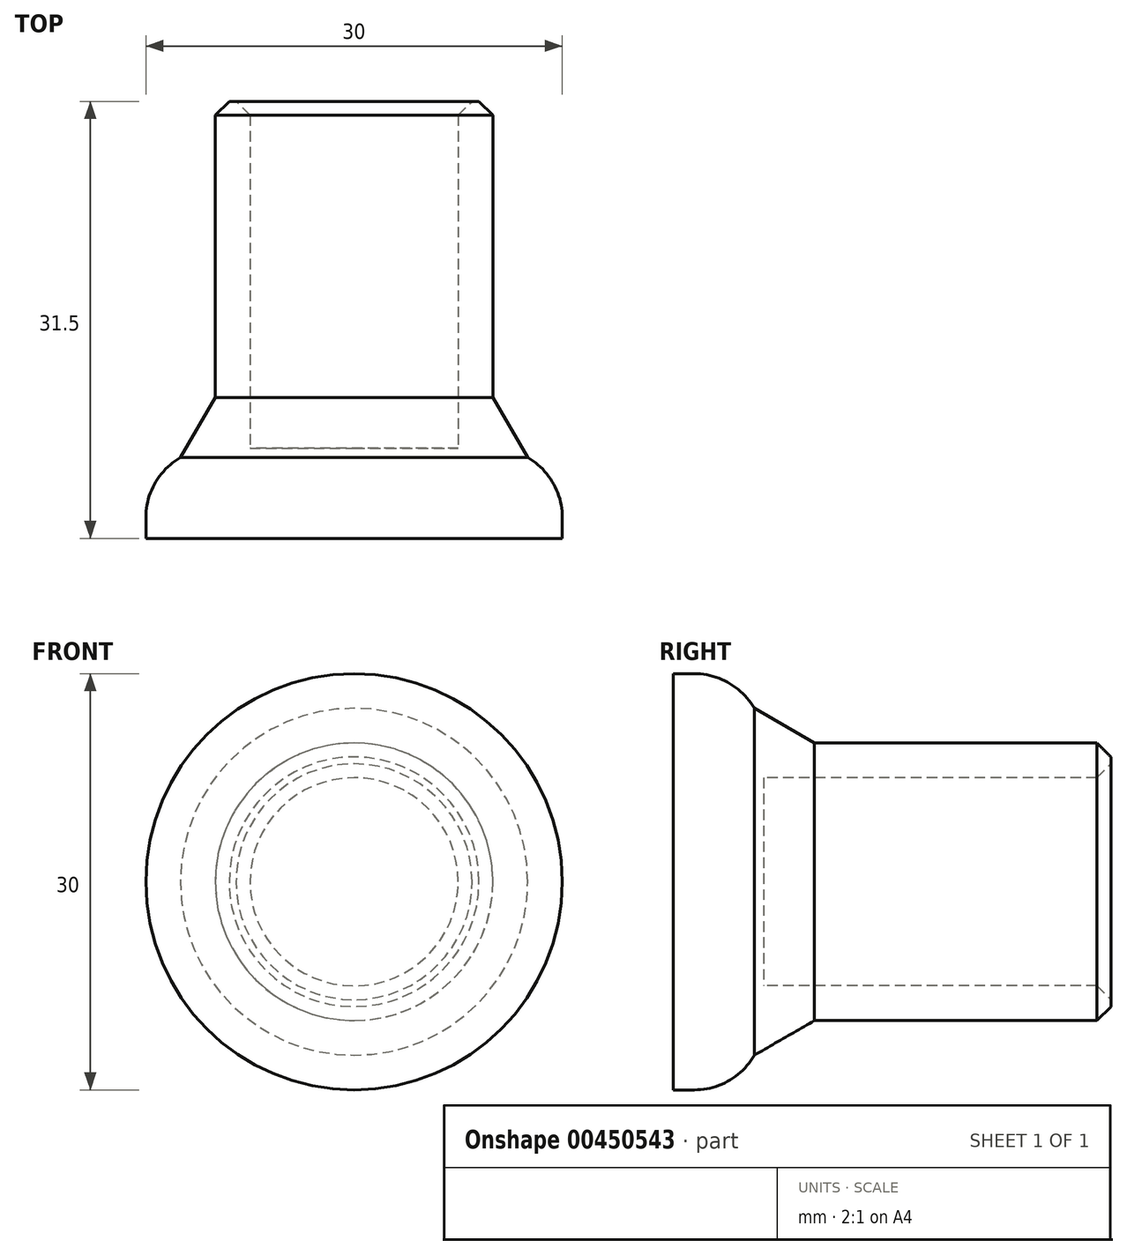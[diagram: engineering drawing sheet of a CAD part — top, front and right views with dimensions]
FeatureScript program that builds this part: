
annotation { "Feature Type Name" : "Feature", "Feature Type Description" : "" }
export const myFeature = defineFeature(function(context is Context, id is Id, definition is map)
    precondition{}
    {
        {
            var Q0;
            Q0=qCreatedBy(makeId("Front.planeOp"),FACE);
            var sketch = newSketch(context, id + "F0", { "sketchPlane" : qUnion([Q0])});
            skCircle(sketch, "E0", {"center": v(0, 0) * mm, "radius": 15 * mm});
            skSolve(sketch);
        }
        {
            var Q0;
            Q0 = qSketchRegion(id + "F0", true);
            extrude(context, id + "F1", {"entities" : qUnion([Q0]), "oppositeDirection" : true, "depth" : 6.5 * mm});
        }
        {
            var Q0;
            Q0=makeQuery(id+"F1.opExtrude","CAP_FACE",FACE,{"disambiguationData":[OSD([sQuery(id+"F0.wireOp",EDGE,"E0")])],"isStart":false});
            fillet(context, id + "F2", {"entities" : qUnion([Q0]), "radius" : 5 * mm, "tangentPropagation" : true, "allowEdgeOverflow" : false});
        }
        {
            var Q0;
            Q0=makeQuery(id+"F1.opExtrude","CAP_FACE",FACE,{"disambiguationData":[OSD([sQuery(id+"F0.wireOp",EDGE,"E0")])],"isStart":false});
            var sketch = newSketch(context, id + "F3", { "sketchPlane" : qUnion([Q0])});
            skCircle(sketch, "E1", {"center": v(0, 0) * mm, "radius": 10 * mm});
            skCircle(sketch, "E2", {"center": v(0, 0) * mm, "radius": 7.5 * mm});
            skSolve(sketch);
        }
        {
            var Q0;
            Q0=makeQuery(id+"F3.imprint","IMPRINT",FACE,{"disambiguationData":[TD([[makeQuery(id+"F3.imprint","IMPRINT",EDGE,{"derivedFrom":sQuery(id+"F3.wireOp",EDGE,"E1")}),1.0]])]});
            extrude(context, id + "F4", {"entities" : qUnion([Q0]), "operationType" : NewBodyOperationType.ADD, "depth" : 25 * mm});
        }
        {
            var Q0;
            Q0=makeQuery(id+"F4.opExtrude","CAP_EDGE",EDGE,{"disambiguationData":[OSD([sQuery(id+"F3.wireOp",EDGE,"E2")])],"isStart":false});
            chamfer(context, id + "F5", {"entities" : qUnion([Q0]), "width" : 1 * mm, "tangentPropagation" : true});
        }
        {
            var Q0;
            Q0=makeQuery(id+"F4.opExtrude","CAP_EDGE",EDGE,{"disambiguationData":[OSD([sQuery(id+"F3.wireOp",EDGE,"E1")])],"isStart":false});
            chamfer(context, id + "F6", {"entities" : qUnion([Q0]), "width" : 1 * mm, "tangentPropagation" : true});
        }
        {
            var Q0;
            {var subQ0=sQuery(id+"F0.wireOp",EDGE,"E0");Q0=makeQuery(id+"F4.boolean.opBoolean","MERGE",EDGE,{"derivedFrom":[makeQuery(id+"F2.opFillet","BLEND_EDGE",EDGE,{"blendedFrom":[makeQuery(id+"F1.opExtrude","CAP_EDGE",EDGE,{"disambiguationData":[OSD([subQ0])],"isStart":false}),makeQuery(id+"F1.opExtrude","CAP_FACE",FACE,{"disambiguationData":[OSD([subQ0])],"isStart":false})],"blendedInto":[makeQuery(id+"F1.opExtrude","CAP_FACE",FACE,{"disambiguationData":[OSD([subQ0])],"isStart":false})]}),makeQuery(id+"F4.opExtrude","CAP_EDGE",EDGE,{"disambiguationData":[OSD([sQuery(id+"F3.wireOp",EDGE,"E1")])],"isStart":true})]});}
            chamfer(context, id + "F7", {"entities" : qUnion([Q0]), "width" : 5 * mm, "tangentPropagation" : true});
        }
    });
